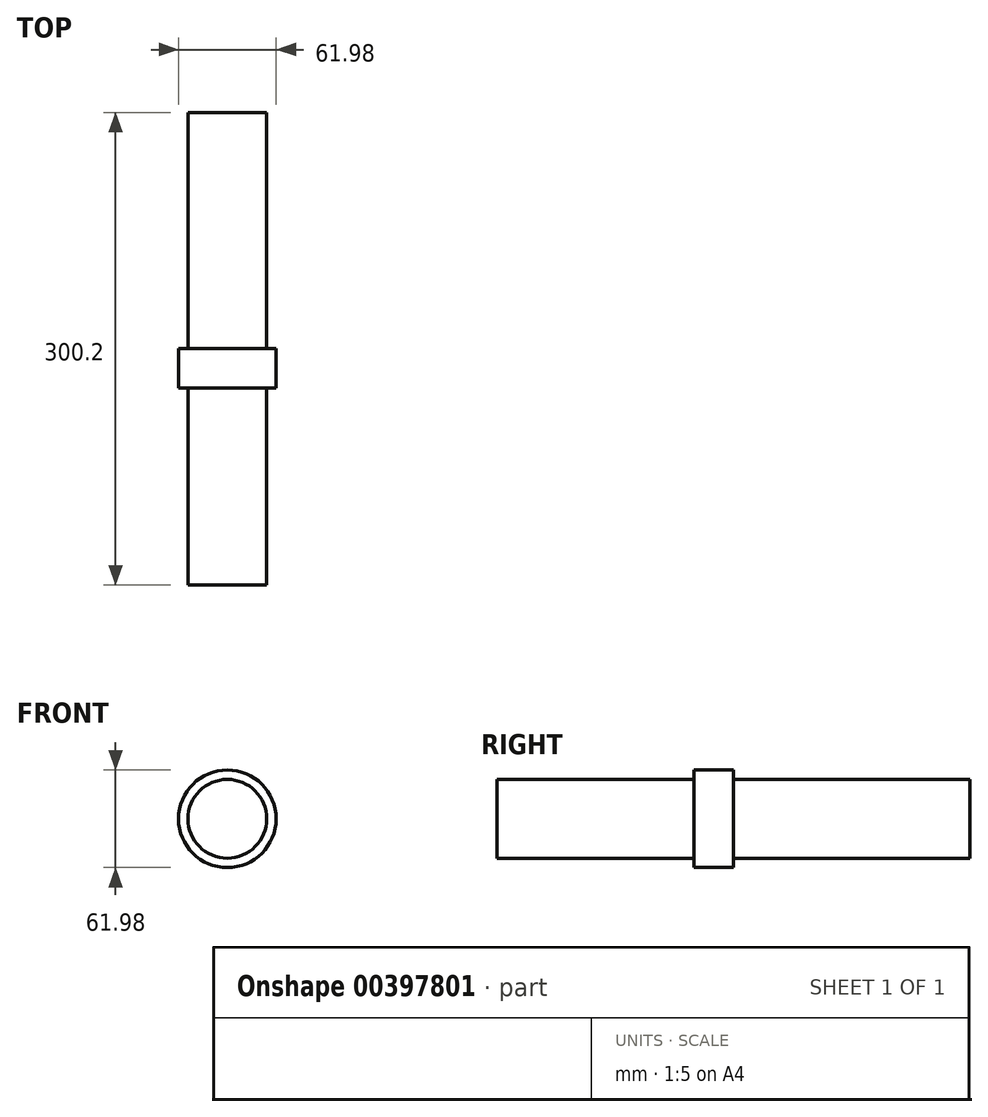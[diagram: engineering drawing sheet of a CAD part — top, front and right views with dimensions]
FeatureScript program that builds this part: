
annotation { "Feature Type Name" : "Feature", "Feature Type Description" : "" }
export const myFeature = defineFeature(function(context is Context, id is Id, definition is map)
    precondition{}
    {
        {
            var Q0;
            Q0=qCreatedBy(makeId("Front.planeOp"),FACE);
            var sketch = newSketch(context, id + "F0", { "sketchPlane" : qUnion([Q0])});
            skCircle(sketch, "E0", {"center": v(0, 0) * mm, "radius": 25 * mm});
            skSolve(sketch);
        }
        {
            var Q0;
            Q0=makeQuery(id+"F0.imprint","IMPRINT",FACE,{"disambiguationData":[TD([[makeQuery(id+"F0.imprint","IMPRINT",EDGE,{"derivedFrom":sQuery(id+"F0.wireOp",EDGE,"E0")}),1.0]])]});
            extrude(context, id + "F1", {"entities" : qUnion([Q0]), "endBound" : BoundingType.SYMMETRIC, "depth" : 300.2 * mm});
        }
        {
            var Q0;
            Q0=qCreatedBy(makeId("Front.planeOp"),FACE);
            var sketch = newSketch(context, id + "F2", { "sketchPlane" : qUnion([Q0])});
            skCircle(sketch, "E1", {"center": v(0, 0) * mm, "radius": 30.99 * mm});
            skCircle(sketch, "E2.0", {"center": v(0, 0) * mm, "radius": 25 * mm});
            skSolve(sketch);
        }
        {
            var Q0;
            Q0=makeQuery(id+"F2.imprint","IMPRINT",FACE,{"disambiguationData":[TD([[makeQuery(id+"F2.imprint","IMPRINT",EDGE,{"derivedFrom":sQuery(id+"F2.wireOp",EDGE,"E1")}),1.0]])]});
            extrude(context, id + "F3", {"entities" : qUnion([Q0]), "operationType" : NewBodyOperationType.ADD, "depth" : 25 * mm});
        }
    });
